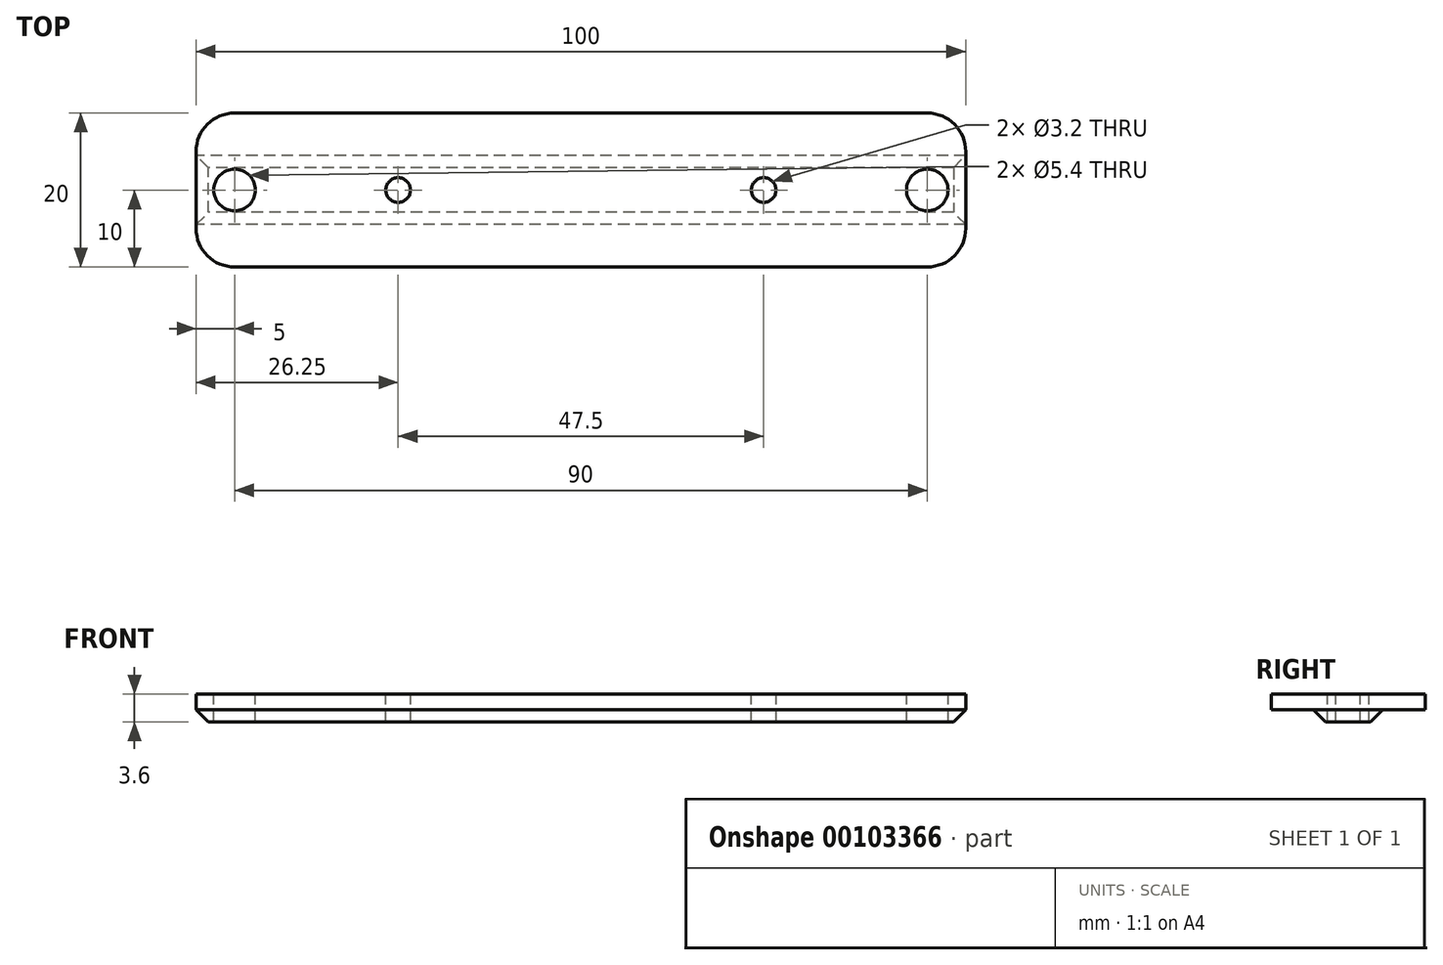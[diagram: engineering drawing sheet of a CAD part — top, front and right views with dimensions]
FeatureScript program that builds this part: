
annotation { "Feature Type Name" : "Feature", "Feature Type Description" : "" }
export const myFeature = defineFeature(function(context is Context, id is Id, definition is map)
    precondition{}
    {
        {
            var Q0;
            Q0=qCreatedBy(makeId("Top.planeOp"),FACE);
            var sketch = newSketch(context, id + "F0", { "sketchPlane" : qUnion([Q0])});
            skLineSegment(sketch, "E0.rect.bottom", {"start": v(45, 10) * mm, "end": v(-45, 10) * mm});
            skLineSegment(sketch, "E0.rect.top", {"start": v(45, -10) * mm, "end": v(-45, -10) * mm});
            skLineSegment(sketch, "E0.rect.left", {"start": v(50, 5) * mm, "end": v(50, -5) * mm});
            skLineSegment(sketch, "E0.rect.right", {"start": v(-50, 5) * mm, "end": v(-50, -5) * mm});
            skPoint(sketch, "E0.rect.middle", {"position": v(0, 0) * mm});
            skPoint(sketch, "E1.visualSharp", {"position": v(-50, 10) * mm});
            skArc(sketch, "E1.filletArc", {"start": v(-45, 10) * mm, "mid": v(-48.54, 8.54) * mm, "end": v(-50, 5) * mm});
            skPoint(sketch, "E2.visualSharp", {"position": v(50, 10) * mm});
            skArc(sketch, "E2.filletArc", {"start": v(50, 5) * mm, "mid": v(48.54, 8.54) * mm, "end": v(45, 10) * mm});
            skPoint(sketch, "E3.visualSharp", {"position": v(50, -10) * mm});
            skArc(sketch, "E3.filletArc", {"start": v(45, -10) * mm, "mid": v(48.54, -8.54) * mm, "end": v(50, -5) * mm});
            skPoint(sketch, "E4.visualSharp", {"position": v(-50, -10) * mm});
            skArc(sketch, "E4.filletArc", {"start": v(-50, -5) * mm, "mid": v(-48.54, -8.54) * mm, "end": v(-45, -10) * mm});
            skSolve(sketch);
        }
        {
            var Q0;
            Q0=qSketchRegion(id+"F0",true);
            extrude(context, id + "F1", {"entities" : qUnion([Q0]), "depth" : 2 * mm});
        }
        {
            var Q0;
            Q0=makeQuery(id+"F1.opExtrude","SWEPT_FACE",FACE,{"disambiguationData":[OSD([sQuery(id+"F0.wireOp",EDGE,"E0.rect.right")])]});
            var sketch = newSketch(context, id + "F2", { "sketchPlane" : qUnion([Q0])});
            skLineSegment(sketch, "E5", {"start": v(0, 0) * mm, "end": v(0, -1.6) * mm, "construction": true});
            skPoint(sketch, "E5.endSnap0", {"position": v(0, 0) * mm});
            skLineSegment(sketch, "E6", {"start": v(-2.9, -1.6) * mm, "end": v(2.9, -1.6) * mm});
            skLineSegment(sketch, "E7", {"start": v(-2.9, -1.6) * mm, "end": v(-4.5, 0) * mm});
            skLineSegment(sketch, "E8", {"start": v(-4.5, 0) * mm, "end": v(4.5, 0) * mm});
            skLineSegment(sketch, "E9", {"start": v(4.5, 0) * mm, "end": v(2.9, -1.6) * mm});
            skSolve(sketch);
        }
        {
            var Q0;
            Q0=qSketchRegion(id+"F2",true);
            var Q1;
            Q1=makeQuery(id+"F1.opExtrude","SWEPT_FACE",FACE,{"disambiguationData":[OSD([sQuery(id+"F0.wireOp",EDGE,"E0.rect.left")])]});
            extrude(context, id + "F3", {"entities" : qUnion([Q0]), "operationType" : NewBodyOperationType.ADD, "endBound" : BoundingType.UP_TO_SURFACE, "oppositeDirection" : true, "endBoundEntityFace" : qUnion([Q1]), "depth" : 25 * mm});
        }
        {
            var Q0;
            Q0=makeQuery(id+"F1.opExtrude","CAP_FACE",FACE,{"disambiguationData":[OSD([sQuery(id+"F0.wireOp",EDGE,"E0.rect.bottom"),sQuery(id+"F0.wireOp",EDGE,"E0.rect.top"),sQuery(id+"F0.wireOp",EDGE,"E0.rect.left"),sQuery(id+"F0.wireOp",EDGE,"E0.rect.right"),sQuery(id+"F0.wireOp",EDGE,"E1.filletArc"),sQuery(id+"F0.wireOp",EDGE,"E2.filletArc"),sQuery(id+"F0.wireOp",EDGE,"E3.filletArc"),sQuery(id+"F0.wireOp",EDGE,"E4.filletArc")])],"isStart":false});
            var sketch = newSketch(context, id + "F4", { "sketchPlane" : qUnion([Q0])});
            skLineSegment(sketch, "E10", {"start": v(-50, 0) * mm, "end": v(-45, 0) * mm, "construction": true});
            skLineSegment(sketch, "E11", {"start": v(-45, 0) * mm, "end": v(-23.75, 0) * mm, "construction": true});
            skLineSegment(sketch, "E12", {"start": v(-23.75, 0) * mm, "end": v(0, 0) * mm, "construction": true});
            skLineSegment(sketch, "E13", {"start": v(0, 0) * mm, "end": v(23.75, 0) * mm, "construction": true});
            skLineSegment(sketch, "E14", {"start": v(23.75, 0) * mm, "end": v(45, 0) * mm, "construction": true});
            skLineSegment(sketch, "E15", {"start": v(45, 0) * mm, "end": v(50, 0) * mm, "construction": true});
            skCircle(sketch, "E16", {"center": v(-45, 0) * mm, "radius": 2.7 * mm});
            skCircle(sketch, "E17", {"center": v(45, 0) * mm, "radius": 2.7 * mm});
            skCircle(sketch, "E18", {"center": v(23.75, 0) * mm, "radius": 1.6 * mm});
            skCircle(sketch, "E19", {"center": v(-23.75, 0) * mm, "radius": 1.6 * mm});
            skSolve(sketch);
        }
        {
            var Q0;
            Q0=qSketchRegion(id+"F4",true);
            extrude(context, id + "F5", {"entities" : qUnion([Q0]), "operationType" : NewBodyOperationType.REMOVE, "endBound" : BoundingType.THROUGH_ALL, "oppositeDirection" : true, "depth" : 25 * mm});
        }
        {
            var Q0;
            Q0=makeQuery(id+"F3.opExtrude","CAP_EDGE",EDGE,{"disambiguationData":[OSD([sQuery(id+"F2.wireOp",EDGE,"E6")])],"isStart":true});
            var Q1;
            Q1=makeQuery(id+"F3.opExtrude","CAP_EDGE",EDGE,{"disambiguationData":[OSD([sQuery(id+"F2.wireOp",EDGE,"E6")])],"isStart":false});
            chamfer(context, id + "F6", {"entities" : qUnion([Q0, Q1]), "width" : 1.6 * mm, "tangentPropagation" : true});
        }
    });
